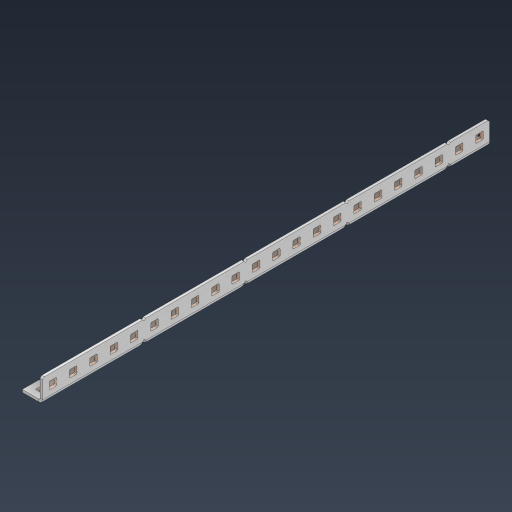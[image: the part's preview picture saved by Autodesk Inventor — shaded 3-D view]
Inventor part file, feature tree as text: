
AUTODESK INVENTOR PART (.ipt)
format: ipt  version: 2024.3 (Build 283343000, 343)  size: 921,600 bytes
history: native  units: in
note: dims shown in document units (in); Inventor stores cm internally (conversion verified against a paired STEP export)
features: other x73, extrude x64, sheet_metal_op x11, pattern_linear x2, mirror x1, chamfer x1, sketch x1
ambient origin geometry x8: Origin, YZ Plane, XZ Plane, XY Plane, X Axis, Y Axis, Z Axis, Center Point
bodies: Solid1 (feature_tree), Body (feature_tree)
feature tree (153):
  sheet_metal_op  "Flanges"
  other  "Flange Pattern Plane"
  other  "Flange Pattern Sketch"
  sheet_metal_op  "Flange Pattern"
  sheet_metal_op  "Body Pattern"
  pattern_linear  "Center Pattern"  Spacing1=11.0in  [1 undecoded]
  other  "Arc Length"
  mirror  "Notch Mirror"
  pattern_linear  "Notch Pattern"  Spacing1=0.0625in  [1 undecoded]
  chamfer  "End Chamfer"
  extrude  "Half Cut"  Depth=0.0625in
  other  "Plate1"
  sketch  "Sketch2"  dims[d0=1.0in d1=11.0in d2=0.0625in d3=0.0625in d4=0.0312in d5=0.125in d6=0.0625in d7=0.5in d8=90.0deg d9=0.0312in d10=0.25in d11=0.0625in d12=0.0625in d16=0.182in d17=0.02in d18=0.0625in d19=0.0in d20=0.25in d21=0.25in d38=8.6614in d40=0.5in d41=0.3937in d43=1.0in d46=0.172in d47=1.0in d48=0.0in d49=0.182in d50=0.02in d51=0.25in d52=0.25in d53=0.0625in d54=0.0in d55=0.172in d56=1.0in d57=0.0in d58=0.25in d60=8.6614in d62=0.5in d63=0.3937in d65=0.5in d85=0.1473in d86=0.1782in d88=0.04in d89=0.0625in d90=0.0in d91=0.04in d92=0.0491in d95=2.5in d96=0.04in d97=0.25in d98=45.0deg d99=0.25in d100=0.5in d101=0.0in d102=2.497in d106=0.182in d107=0.02in d108=0.5in d109=0.5in d110=0.0625in d111=0.0in d112=0.172in d113=0.5in d114=0.0in d117=0.5in d118=0.5in d119=0.5in]
  other  "Plate2"
  sheet_metal_op  "Bend1"
  sheet_metal_op  "Corner1"
  other  "Srf1"
  other  "Srf2"
  other  "Srf91"
  sheet_metal_op  "Body Pattern Sketch"
  other  "Srf92"
  other  "Srf786"
  other  "Srf823"
  other  "Srf824"
  other  "Srf825"
  other  "Srf826"
  other  "Srf827"
  other  "Srf828"
  other  "Srf829"
  other  "Srf856"
  other  "Srf857"
  other  "Srf858"
  other  "Srf859"
  other  "Srf860"
  other  "Srf861"
  other  "Srf862"
  other  "Srf889"
  other  "Srf890"
  other  "Srf891"
  other  "Srf892"
  other  "Srf893"
  other  "Srf894"
  other  "Srf895"
  other  "Srf896"
  other  "Srf922"
  other  "Srf923"
  other  "Srf924"
  other  "Srf925"
  other  "Srf926"
  other  "Srf959"
  other  "Srf960"
  other  "Srf961"
  other  "Srf962"
  other  "Srf963"
  other  "Srf996"
  other  "Srf997"
  other  "Srf998"
  other  "Srf999"
  other  "Srf1000"
  other  "Srf1143"
  other  "Srf1144"
  other  "Srf1145"
  other  "Srf1146"
  other  "Srf1147"
  other  "Srf1148"
  other  "Srf1149"
  other  "Srf1150"
  other  "Srf1199"
  other  "Srf1200"
  other  "Srf1201"
  other  "Srf1202"
  other  "Srf1203"
  other  "Srf1204"
  other  "Srf1205"
  other  "Srf1206"
  other  "Srf1255"
  other  "Srf1256"
  other  "Srf1257"
  other  "Srf1258"
  other  "Srf1259"
  other  "Srf1260"
  other  "Srf1261"
  other  "Srf1262"
  sheet_metal_op  "Flange Stamp"
  sheet_metal_op  "Flange Circle"
  sheet_metal_op  "Body Stamp"
  sheet_metal_op  "Body Circle"
  other  "Center Stamp"
  other  "Center Circle"
  sheet_metal_op  "Notch"
  extrude  "ExtrusionSrf2"  Depth=0.0312in
  extrude  "ExtrusionSrf92"  Depth=0.5in
  extrude  "ExtrusionSrf823"  Depth=0.0625in
  extrude  "ExtrusionSrf824"  Depth=0.5in TaperAngle=90.0deg
  extrude  "ExtrusionSrf825"  Depth=0.25in
  extrude  "ExtrusionSrf826"  Depth=0.0625in
  extrude  "ExtrusionSrf827"  Depth=0.0625in
  extrude  "ExtrusionSrf828"  Depth=0.182in
  extrude  "ExtrusionSrf829"  Depth=0.02in
  extrude  "ExtrusionSrf856"  Depth=0.0625in
  extrude  "ExtrusionSrf857"  TaperAngle=0.0deg  [1 undecoded]
  extrude  "ExtrusionSrf858"  Depth=0.25in
  extrude  "ExtrusionSrf859"  Depth=0.25in
  extrude  "ExtrusionSrf860"  Depth=0.5in
  extrude  "ExtrusionSrf861"  Depth=0.5in
  extrude  "ExtrusionSrf862"  Depth=1.0in TaperAngle=0.0deg
  extrude  "ExtrusionSrf889"  Depth=0.182in
  extrude  "ExtrusionSrf890"  Depth=0.02in
  extrude  "ExtrusionSrf891"  Depth=0.25in
  extrude  "ExtrusionSrf892"  Depth=0.25in
  extrude  "ExtrusionSrf893"  Depth=0.0625in
  extrude  "ExtrusionSrf894"  TaperAngle=0.0deg  [1 undecoded]
  extrude  "ExtrusionSrf895"  Depth=0.5in
  extrude  "ExtrusionSrf896"  Depth=1.0in TaperAngle=0.0deg
  extrude  "ExtrusionSrf922"  Depth=0.25in
  extrude  "ExtrusionSrf923"  Depth=0.5in
  extrude  "ExtrusionSrf924"  Depth=0.5in
  extrude  "ExtrusionSrf925"  Depth=0.5in
  extrude  "ExtrusionSrf926"  Depth=0.5in
  extrude  "ExtrusionSrf959"  Depth=0.5in
  extrude  "ExtrusionSrf960"  Depth=0.0625in
  extrude  "ExtrusionSrf961"  TaperAngle=0.0deg  [1 undecoded]
  extrude  "ExtrusionSrf962"  Depth=0.5in
  extrude  "ExtrusionSrf963"  Depth=0.5in
  extrude  "ExtrusionSrf996"  Depth=2.5in
  extrude  "ExtrusionSrf997"  Depth=0.25in TaperAngle=45.0deg
  extrude  "ExtrusionSrf998"  Depth=0.25in
  extrude  "ExtrusionSrf999"  Depth=0.5in TaperAngle=0.0deg
  extrude  "ExtrusionSrf1000"  Depth=0.5in
  extrude  "ExtrusionSrf1143"  Depth=0.182in
  extrude  "ExtrusionSrf1144"  Depth=0.02in
  extrude  "ExtrusionSrf1145"  Depth=0.5in
  extrude  "ExtrusionSrf1146"  Depth=0.5in
  extrude  "ExtrusionSrf1147"  Depth=0.0625in
  extrude  "ExtrusionSrf1148"  TaperAngle=0.0deg  [1 undecoded]
  extrude  "ExtrusionSrf1149"  Depth=0.5in
  extrude  "ExtrusionSrf1150"  Depth=0.5in TaperAngle=0.0deg
  extrude  "ExtrusionSrf1199"  Depth=0.5in
  extrude  "ExtrusionSrf1200"  Depth=0.5in
  extrude  "ExtrusionSrf1201"  Depth=0.5in
  extrude  "ExtrusionSrf1202"  [1 undecoded]
  extrude  "ExtrusionSrf1203"  [1 undecoded]
  extrude  "ExtrusionSrf1204"  [1 undecoded]
  extrude  "ExtrusionSrf1205"  [1 undecoded]
  extrude  "ExtrusionSrf1206"  [1 undecoded]
  extrude  "ExtrusionSrf1255"  [1 undecoded]
  extrude  "ExtrusionSrf1256"  [1 undecoded]
  extrude  "ExtrusionSrf1257"  [1 undecoded]
  extrude  "ExtrusionSrf1258"  [1 undecoded]
  extrude  "ExtrusionSrf1259"  [1 undecoded]
  extrude  "ExtrusionSrf1260"  [1 undecoded]
  extrude  "ExtrusionSrf1261"  [1 undecoded]
  extrude  "ExtrusionSrf1262"  [1 undecoded]
note: 19 required parameter values undecoded (feature->parameter linkage not recoverable at this tier; creation-order binding heuristic only, values carry confidence <= 0.55)
